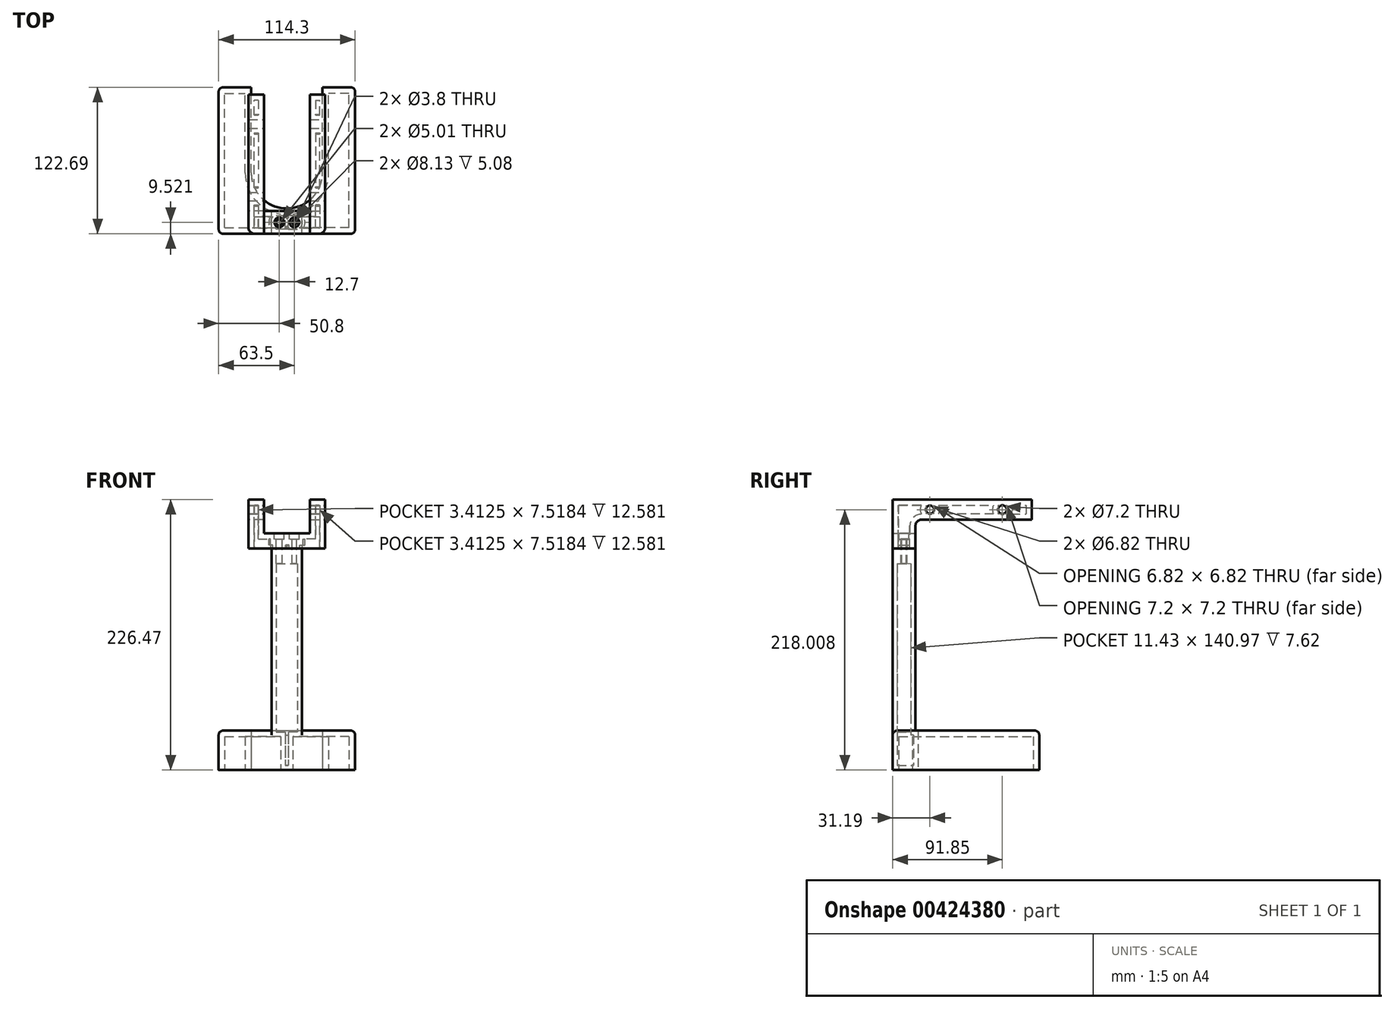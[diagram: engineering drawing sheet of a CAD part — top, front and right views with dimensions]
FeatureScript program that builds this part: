
annotation { "Feature Type Name" : "Feature", "Feature Type Description" : "" }
export const myFeature = defineFeature(function(context is Context, id is Id, definition is map)
    precondition{}
    {
        {
            var Q0;
            Q0=qCreatedBy(makeId("Top.planeOp"),FACE);
            var sketch = newSketch(context, id + "F0", { "sketchPlane" : qUnion([Q0])});
            skLineSegment(sketch, "E0", {"start": v(57.15, -21.2) * mm, "end": v(57.15, 101.5) * mm});
            skLineSegment(sketch, "E1", {"start": v(29.87, 29.87) * mm, "end": v(29.87, 101.5) * mm});
            skLineSegment(sketch, "E2", {"start": v(57.15, 101.5) * mm, "end": v(29.87, 101.5) * mm});
            skLineSegment(sketch, "E3", {"start": v(57.15, -21.2) * mm, "end": v(0, -21.2) * mm});
            skLineSegment(sketch, "E4", {"start": v(0, -21.2) * mm, "end": v(0, 0) * mm});
            skPoint(sketch, "E5.center.orphan", {"position": v(0, 29.87) * mm});
            skArc(sketch, "E6", {"start": v(0, 0) * mm, "mid": v(21.12, 8.75) * mm, "end": v(29.87, 29.87) * mm});
            skSolve(sketch);
        }
        {
            var Q0;
            Q0=makeQuery(id+"F0.imprint","IMPRINT",FACE,{"disambiguationData":[TD([[makeQuery(id+"F0.imprint","IMPRINT",EDGE,{"derivedFrom":sQuery(id+"F0.wireOp",EDGE,"E0")}),1.0]])]});
            extrude(context, id + "F1", {"entities" : qUnion([Q0]), "depth" : 33.02 * mm});
        }
        {
            var Q0;
            Q0=makeQuery(id+"F1.opExtrude","CAP_FACE",FACE,{"disambiguationData":[OSD([sQuery(id+"F0.wireOp",EDGE,"E0"),sQuery(id+"F0.wireOp",EDGE,"E1"),sQuery(id+"F0.wireOp",EDGE,"E2"),sQuery(id+"F0.wireOp",EDGE,"E3"),sQuery(id+"F0.wireOp",EDGE,"E4"),sQuery(id+"F0.wireOp",EDGE,"E6")])],"isStart":true});
            shell(context, id + "F2", {"entities" : qUnion([Q0]), "thickness" : 5.08 * mm});
        }
        {
            var Q0;
            Q0=makeQuery(id+"F1.opExtrude","CAP_FACE",FACE,{"disambiguationData":[OSD([sQuery(id+"F0.wireOp",EDGE,"E0"),sQuery(id+"F0.wireOp",EDGE,"E1"),sQuery(id+"F0.wireOp",EDGE,"E2"),sQuery(id+"F0.wireOp",EDGE,"E3"),sQuery(id+"F0.wireOp",EDGE,"E4"),sQuery(id+"F0.wireOp",EDGE,"E6")])],"isStart":false});
            var sketch = newSketch(context, id + "F3", { "sketchPlane" : qUnion([Q0])});
            skLineSegment(sketch, "E7.bottom", {"start": v(0, -21.2) * mm, "end": v(12.7, -21.2) * mm});
            skLineSegment(sketch, "E7.top", {"start": v(0, -2.14) * mm, "end": v(12.7, -2.14) * mm});
            skLineSegment(sketch, "E7.left", {"start": v(0, -21.2) * mm, "end": v(0, -2.14) * mm});
            skLineSegment(sketch, "E7.right", {"start": v(12.7, -21.2) * mm, "end": v(12.7, -2.14) * mm});
            skSolve(sketch);
        }
        {
            var Q0;
            Q0=makeQuery(id+"F3.imprint","IMPRINT",FACE,{"disambiguationData":[TD([[makeQuery(id+"F3.imprint","IMPRINT",EDGE,{"derivedFrom":sQuery(id+"F3.wireOp",EDGE,"E7.bottom")}),-1.0]])]});
            extrude(context, id + "F4", {"entities" : qUnion([Q0]), "operationType" : NewBodyOperationType.ADD, "depth" : 152.4 * mm});
        }
        {
            var Q0;
            Q0=makeQuery(id+"F4.opExtrude","CAP_EDGE",EDGE,{"disambiguationData":[OSD([sQuery(id+"F3.wireOp",EDGE,"E7.top")])],"isStart":true});
            var Q1;
            Q1=makeQuery(id+"F4.opExtrude","CAP_EDGE",EDGE,{"disambiguationData":[OSD([sQuery(id+"F3.wireOp",EDGE,"E7.right")])],"isStart":true});
            var Q2;
            Q2=makeQuery(id+"F1.opExtrude","CAP_EDGE",EDGE,{"disambiguationData":[OSD([sQuery(id+"F0.wireOp",EDGE,"E3")])],"isStart":false});
            var Q3;
            Q3=makeQuery(id+"F1.opExtrude","CAP_EDGE",EDGE,{"disambiguationData":[OSD([sQuery(id+"F0.wireOp",EDGE,"E0")])],"isStart":false});
            var Q4;
            Q4=makeQuery(id+"F1.opExtrude","CAP_EDGE",EDGE,{"disambiguationData":[OSD([sQuery(id+"F0.wireOp",EDGE,"E2")])],"isStart":false});
            var Q5;
            Q5=makeQuery(id+"F1.opExtrude","SWEPT_EDGE",EDGE,{"disambiguationData":[OSD([sQuery(id+"F0.wireOp",EDGE,"E0"),sQuery(id+"F0.wireOp",EDGE,"E3")])]});
            var Q6;
            Q6=makeQuery(id+"F1.opExtrude","SWEPT_EDGE",EDGE,{"disambiguationData":[OSD([sQuery(id+"F0.wireOp",EDGE,"E0"),sQuery(id+"F0.wireOp",EDGE,"E2")])]});
            fillet(context, id + "F5", {"entities" : qUnion([Q0, Q1, Q2, Q3, Q4, Q5, Q6]), "radius" : 3.8 * mm, "tangentPropagation" : true, "allowEdgeOverflow" : false});
        }
        {
            var Q0;
            Q0=makeQuery(id+"F1.opExtrude","SWEPT_BODY",BODY,{"disambiguationData":[OSD([sQuery(id+"F0.wireOp",EDGE,"E0"),sQuery(id+"F0.wireOp",EDGE,"E1"),sQuery(id+"F0.wireOp",EDGE,"E2"),sQuery(id+"F0.wireOp",EDGE,"E3"),sQuery(id+"F0.wireOp",EDGE,"E4"),sQuery(id+"F0.wireOp",EDGE,"E6")])]});
            var Q1;
            Q1=makeQuery(id+"F4.boolean.opBoolean","MERGE",FACE,{"derivedFrom":[makeQuery(id+"F1.opExtrude","SWEPT_FACE",FACE,{"disambiguationData":[OSD([sQuery(id+"F0.wireOp",EDGE,"E4")])]}),makeQuery(id+"F4.opExtrude","SWEPT_FACE",FACE,{"disambiguationData":[OSD([sQuery(id+"F3.wireOp",EDGE,"E7.left")])]})]});
            mirror(context, id + "F6", {"operationType" : NewBodyOperationType.ADD, "entities" : qUnion([Q0]), "mirrorPlane" : qUnion([Q1])});
        }
        {
            var Q0;
            {var subQ0=makeQuery(id+"F4.opExtrude","CAP_FACE",FACE,{"disambiguationData":[OSD([sQuery(id+"F3.wireOp",EDGE,"E7.bottom"),sQuery(id+"F3.wireOp",EDGE,"E7.top"),sQuery(id+"F3.wireOp",EDGE,"E7.left"),sQuery(id+"F3.wireOp",EDGE,"E7.right")])],"isStart":false});Q0=makeQuery(id+"F6.boolean.opBoolean","MERGE",FACE,{"derivedFrom":[subQ0,makeQuery(id+"F6.opPattern","COPY",FACE,{"derivedFrom":subQ0,"instanceName":"1"})]});}
            shell(context, id + "F7", {"entities" : qUnion([Q0]), "thickness" : 3.8 * mm});
        }
        {
            var Q0;
            {var subQ0=makeQuery(id+"F4.opExtrude","CAP_FACE",FACE,{"disambiguationData":[OSD([sQuery(id+"F3.wireOp",EDGE,"E7.bottom"),sQuery(id+"F3.wireOp",EDGE,"E7.top"),sQuery(id+"F3.wireOp",EDGE,"E7.left"),sQuery(id+"F3.wireOp",EDGE,"E7.right")])],"isStart":false});Q0=makeQuery(id+"F6.boolean.opBoolean","MERGE",FACE,{"derivedFrom":[subQ0,makeQuery(id+"F6.opPattern","COPY",FACE,{"derivedFrom":subQ0,"instanceName":"1"})]});}
            var sketch = newSketch(context, id + "F8", { "sketchPlane" : qUnion([Q0])});
            skLineSegment(sketch, "E8.0", {"start": v(-8.9, -17.38) * mm, "end": v(-8.9, -5.95) * mm});
            skLineSegment(sketch, "E9.0", {"start": v(-8.89, -5.95) * mm, "end": v(8.89, -5.95) * mm});
            skLineSegment(sketch, "E10.0", {"start": v(8.89, -17.38) * mm, "end": v(-8.89, -17.38) * mm});
            skLineSegment(sketch, "E11.0", {"start": v(8.9, -17.38) * mm, "end": v(8.89, -5.95) * mm});
            skSolve(sketch);
        }
        {
            var Q0;
            Q0=makeQuery(id+"F8.imprint","IMPRINT",FACE,{"disambiguationData":[TD([[makeQuery(id+"F8.imprint","IMPRINT",EDGE,{"derivedFrom":sQuery(id+"F8.wireOp",EDGE,"E8.0")}),-1.0]])]});
            extrude(context, id + "F9", {"entities" : qUnion([Q0]), "operationType" : NewBodyOperationType.ADD, "oppositeDirection" : true, "depth" : 12.7 * mm});
        }
        {
            var Q0;
            {var subQ0=makeQuery(id+"F4.opExtrude","CAP_FACE",FACE,{"disambiguationData":[OSD([sQuery(id+"F3.wireOp",EDGE,"E7.bottom"),sQuery(id+"F3.wireOp",EDGE,"E7.top"),sQuery(id+"F3.wireOp",EDGE,"E7.left"),sQuery(id+"F3.wireOp",EDGE,"E7.right")])],"isStart":false});Q0=makeQuery(id+"F9.boolean.opBoolean","MERGE",FACE,{"derivedFrom":[makeQuery(id+"F6.boolean.opBoolean","MERGE",FACE,{"derivedFrom":[subQ0,makeQuery(id+"F6.opPattern","COPY",FACE,{"derivedFrom":subQ0,"instanceName":"1"})]}),makeQuery(id+"F9.opExtrude","CAP_FACE",FACE,{"disambiguationData":[OSD([sQuery(id+"F8.wireOp",EDGE,"E8.0"),sQuery(id+"F8.wireOp",EDGE,"E9.0"),sQuery(id+"F8.wireOp",EDGE,"E10.0"),sQuery(id+"F8.wireOp",EDGE,"E11.0")])],"isStart":true})]});}
            var sketch = newSketch(context, id + "F10", { "sketchPlane" : qUnion([Q0])});
            skLineSegment(sketch, "E12", {"start": v(0, -2.14) * mm, "end": v(19.28, -2.14) * mm});
            skLineSegment(sketch, "E13", {"start": v(19.28, -2.14) * mm, "end": v(19.28, 95.34) * mm});
            skLineSegment(sketch, "E14", {"start": v(19.28, 95.34) * mm, "end": v(32.1, 95.34) * mm});
            skLineSegment(sketch, "E15", {"start": v(32.1, 95.34) * mm, "end": v(32.1, -21.2) * mm});
            skLineSegment(sketch, "E16", {"start": v(32.1, -21.2) * mm, "end": v(0, -21.2) * mm});
            skLineSegment(sketch, "E17", {"start": v(0, -21.2) * mm, "end": v(0, -2.14) * mm});
            skSolve(sketch);
        }
        {
            var Q0;
            {var subQ1=sQuery(id+"F10.wireOp",EDGE,"E13");Q0=makeQuery(id+"F10.imprint","IMPRINT",FACE,{"disambiguationData":[TD([[makeQuery(id+"F10.imprint","IMPRINT",EDGE,{"derivedFrom":subQ1}),-1.0]])]});}
            var Q1;
            {var subQ4=sQuery(id+"F10.wireOp",EDGE,"E17");Q1=makeQuery(id+"F10.imprint","IMPRINT",FACE,{"disambiguationData":[TD([[makeQuery(id+"F10.imprint","IMPRINT",EDGE,{"derivedFrom":subQ4}),-1.0]])]});}
            extrude(context, id + "F11", {"entities" : qUnion([Q0, Q1]), "depth" : 43.18 * mm});
        }
        {
            var Q0;
            Q0=makeQuery(id+"F11.opExtrude","SWEPT_FACE",FACE,{"disambiguationData":[OSD([sQuery(id+"F10.wireOp",EDGE,"E15")])]});
            var sketch = newSketch(context, id + "F12", { "sketchPlane" : qUnion([Q0])});
            skPoint(sketch, "E18.0", {"position": v(-2.14, 185.42) * mm});
            skLineSegment(sketch, "E19.bottom", {"start": v(-2.14, 185.42) * mm, "end": v(95.34, 185.42) * mm});
            skLineSegment(sketch, "E19.top", {"start": v(-2.14, 209.55) * mm, "end": v(95.34, 209.55) * mm});
            skLineSegment(sketch, "E19.left", {"start": v(-2.14, 185.42) * mm, "end": v(-2.14, 209.55) * mm});
            skLineSegment(sketch, "E19.right", {"start": v(95.34, 185.42) * mm, "end": v(95.34, 209.55) * mm});
            skSolve(sketch);
        }
        {
            var Q0;
            Q0=makeQuery(id+"F12.imprint","IMPRINT",FACE,{"disambiguationData":[TD([[makeQuery(id+"F12.imprint","IMPRINT",EDGE,{"derivedFrom":sQuery(id+"F12.wireOp",EDGE,"E19.bottom")}),-1.0]])]});
            extrude(context, id + "F13", {"entities" : qUnion([Q0]), "operationType" : NewBodyOperationType.REMOVE, "endBound" : BoundingType.THROUGH_ALL, "oppositeDirection" : true, "depth" : 25.4 * mm});
        }
        {
            var Q0;
            Q0=makeQuery(id+"F13.boolean.opBoolean","MERGE",FACE,{"derivedFrom":[makeQuery(id+"F11.opExtrude","SWEPT_FACE",FACE,{"disambiguationData":[OSD([sQuery(id+"F10.wireOp",EDGE,"E12")])]}),makeQuery(id+"F13.opExtrude","SWEPT_FACE",FACE,{"disambiguationData":[OSD([sQuery(id+"F12.wireOp",EDGE,"E19.left")])]})]});
            var sketch = newSketch(context, id + "F14", { "sketchPlane" : qUnion([Q0])});
            skLineSegment(sketch, "E20.bottom", {"start": v(-19.28, 228.6) * mm, "end": v(0, 228.6) * mm});
            skLineSegment(sketch, "E20.top", {"start": v(-19.28, 198.12) * mm, "end": v(0, 198.12) * mm});
            skLineSegment(sketch, "E20.left", {"start": v(-19.28, 228.6) * mm, "end": v(-19.28, 198.12) * mm});
            skLineSegment(sketch, "E20.right", {"start": v(0, 228.6) * mm, "end": v(0, 198.12) * mm});
            skSolve(sketch);
        }
        {
            var Q0;
            {var subQ1=sQuery(id+"F14.wireOp",EDGE,"E20.bottom");Q0=makeQuery(id+"F14.imprint","IMPRINT",FACE,{"disambiguationData":[TD([[makeQuery(id+"F14.imprint","IMPRINT",EDGE,{"derivedFrom":subQ1}),1.0]])]});}
            extrude(context, id + "F15", {"entities" : qUnion([Q0]), "operationType" : NewBodyOperationType.REMOVE, "oppositeDirection" : true, "depth" : 25.4 * mm});
        }
        {
            var Q0;
            Q0=makeQuery(id+"F11.opExtrude","SWEPT_EDGE",EDGE,{"disambiguationData":[OSD([sQuery(id+"F10.wireOp",EDGE,"E15"),sQuery(id+"F10.wireOp",EDGE,"E16")])]});
            var Q1;
            Q1=makeQuery(id+"F13.boolean.opBoolean","COPY",EDGE,{"derivedFrom":makeQuery(id+"F13.opExtrude","CAP_EDGE",EDGE,{"disambiguationData":[OSD([sQuery(id+"F12.wireOp",EDGE,"E19.left")])],"isStart":true})});
            fillet(context, id + "F16", {"entities" : qUnion([Q0, Q1]), "radius" : 5.08 * mm, "tangentPropagation" : true, "allowEdgeOverflow" : false});
        }
        {
            var Q0;
            Q0=makeQuery(id+"F15.boolean.opBoolean","COPY",FACE,{"derivedFrom":makeQuery(id+"F15.opExtrude","SWEPT_FACE",FACE,{"disambiguationData":[OSD([sQuery(id+"F14.wireOp",EDGE,"E20.top")])]})});
            var sketch = newSketch(context, id + "F17", { "sketchPlane" : qUnion([Q0])});
            skCircle(sketch, "E21", {"center": v(6.35, -11.67) * mm, "radius": 1.9 * mm});
            skSolve(sketch);
        }
        {
            var Q0;
            Q0=makeQuery(id+"F17.imprint","IMPRINT",FACE,{"disambiguationData":[TD([[makeQuery(id+"F17.imprint","IMPRINT",EDGE,{"derivedFrom":sQuery(id+"F17.wireOp",EDGE,"E21")}),1.0]])]});
            var Q1;
            Q1=sQuery(id+"F17.wireOp",EDGE,"E21");
            extrude(context, id + "F18", {"entities" : qUnion([Q0]), "operationType" : NewBodyOperationType.REMOVE, "surfaceEntities" : qUnion([Q1]), "oppositeDirection" : true, "depth" : 79 * mm});
        }
        {
            var Q0;
            Q0=qCreatedBy(makeId("Front.planeOp"),FACE);
            var sketch = newSketch(context, id + "F19", { "sketchPlane" : qUnion([Q0])});
            skLineSegment(sketch, "E22.bottom", {"start": v(0, 210.43) * mm, "end": v(-135.66, 210.43) * mm});
            skLineSegment(sketch, "E22.top", {"start": v(0, -60.9) * mm, "end": v(-135.66, -60.9) * mm});
            skLineSegment(sketch, "E22.left", {"start": v(0, 210.43) * mm, "end": v(0, -60.9) * mm});
            skLineSegment(sketch, "E22.right", {"start": v(-135.66, 210.43) * mm, "end": v(-135.66, -60.9) * mm});
            skSolve(sketch);
        }
        {
            var Q0;
            Q0=makeQuery(id+"F19.imprint","IMPRINT",FACE,{"disambiguationData":[TD([[makeQuery(id+"F19.imprint","IMPRINT",EDGE,{"derivedFrom":sQuery(id+"F19.wireOp",EDGE,"E22.bottom")}),1.0]])]});
            extrude(context, id + "F20", {"entities" : qUnion([Q0]), "operationType" : NewBodyOperationType.REMOVE, "depth" : 127 * mm, "hasSecondDirection" : true, "secondDirectionOppositeDirection" : true, "secondDirectionDepth" : 127 * mm});
        }
        {
            var Q0;
            Q0=makeQuery(id+"F11.opExtrude","SWEPT_BODY",BODY,{"disambiguationData":[OSD([sQuery(id+"F10.wireOp",EDGE,"E12"),sQuery(id+"F10.wireOp",EDGE,"E13"),sQuery(id+"F10.wireOp",EDGE,"E14"),sQuery(id+"F10.wireOp",EDGE,"E15"),sQuery(id+"F10.wireOp",EDGE,"E16"),sQuery(id+"F10.wireOp",EDGE,"E17")])]});
            var Q1;
            Q1=makeQuery(id+"F1.opExtrude","SWEPT_BODY",BODY,{"disambiguationData":[OSD([sQuery(id+"F0.wireOp",EDGE,"E0"),sQuery(id+"F0.wireOp",EDGE,"E1"),sQuery(id+"F0.wireOp",EDGE,"E2"),sQuery(id+"F0.wireOp",EDGE,"E3"),sQuery(id+"F0.wireOp",EDGE,"E4"),sQuery(id+"F0.wireOp",EDGE,"E6")])]});
            var Q2;
            Q2=makeQuery(id+"F11.opExtrude","SWEPT_FACE",FACE,{"disambiguationData":[OSD([sQuery(id+"F10.wireOp",EDGE,"E17")])]});
            mirror(context, id + "F21", {"entities" : qUnion([Q0, Q1]), "mirrorPlane" : qUnion([Q2])});
        }
        {
            var Q0;
            Q0=makeQuery(id+"F1.opExtrude","SWEPT_BODY",BODY,{"disambiguationData":[OSD([sQuery(id+"F0.wireOp",EDGE,"E0"),sQuery(id+"F0.wireOp",EDGE,"E1"),sQuery(id+"F0.wireOp",EDGE,"E2"),sQuery(id+"F0.wireOp",EDGE,"E3"),sQuery(id+"F0.wireOp",EDGE,"E4"),sQuery(id+"F0.wireOp",EDGE,"E6")])]});
            var Q1;
            Q1=makeQuery(id+"F21.opPattern","COPY",BODY,{"derivedFrom":makeQuery(id+"F1.opExtrude","SWEPT_BODY",BODY,{"disambiguationData":[OSD([sQuery(id+"F0.wireOp",EDGE,"E0"),sQuery(id+"F0.wireOp",EDGE,"E1"),sQuery(id+"F0.wireOp",EDGE,"E2"),sQuery(id+"F0.wireOp",EDGE,"E3"),sQuery(id+"F0.wireOp",EDGE,"E4"),sQuery(id+"F0.wireOp",EDGE,"E6")])]}),"instanceName":"1"});
            booleanBodies(context, id + "F22", {"operationType" : BooleanOperationType.UNION, "tools" : qUnion([Q0, Q1])});
        }
        {
            var Q0;
            Q0=makeQuery(id+"F11.opExtrude","SWEPT_BODY",BODY,{"disambiguationData":[OSD([sQuery(id+"F10.wireOp",EDGE,"E12"),sQuery(id+"F10.wireOp",EDGE,"E13"),sQuery(id+"F10.wireOp",EDGE,"E14"),sQuery(id+"F10.wireOp",EDGE,"E15"),sQuery(id+"F10.wireOp",EDGE,"E16"),sQuery(id+"F10.wireOp",EDGE,"E17")])]});
            var Q1;
            Q1=makeQuery(id+"F21.opPattern","COPY",BODY,{"derivedFrom":makeQuery(id+"F11.opExtrude","SWEPT_BODY",BODY,{"disambiguationData":[OSD([sQuery(id+"F10.wireOp",EDGE,"E12"),sQuery(id+"F10.wireOp",EDGE,"E13"),sQuery(id+"F10.wireOp",EDGE,"E14"),sQuery(id+"F10.wireOp",EDGE,"E15"),sQuery(id+"F10.wireOp",EDGE,"E16"),sQuery(id+"F10.wireOp",EDGE,"E17")])]}),"instanceName":"1"});
            booleanBodies(context, id + "F23", {"operationType" : BooleanOperationType.UNION, "tools" : qUnion([Q0, Q1])});
        }
        {
            var Q0;
            Q0=makeQuery(id+"F11.opExtrude","SWEPT_FACE",FACE,{"disambiguationData":[OSD([sQuery(id+"F10.wireOp",EDGE,"E15")])]});
            var sketch = newSketch(context, id + "F24", { "sketchPlane" : qUnion([Q0])});
            skLineSegment(sketch, "E23", {"start": v(0, 0) * mm, "end": v(0, 33.4) * mm, "construction": true});
            skCircle(sketch, "E24", {"center": v(10, 218) * mm, "radius": 3.4 * mm});
            skCircle(sketch, "E25", {"center": v(70.66, 218) * mm, "radius": 3.6 * mm});
            skPoint(sketch, "E25.centerSnap0", {"position": v(95.34, 218) * mm});
            skSolve(sketch);
        }
        {
            var Q0;
            Q0=makeQuery(id+"F24.imprint","IMPRINT",FACE,{"disambiguationData":[TD([[makeQuery(id+"F24.imprint","IMPRINT",EDGE,{"derivedFrom":sQuery(id+"F24.wireOp",EDGE,"E24")}),1.0]])]});
            var Q1;
            Q1=makeQuery(id+"F24.imprint","IMPRINT",FACE,{"disambiguationData":[TD([[makeQuery(id+"F24.imprint","IMPRINT",EDGE,{"derivedFrom":sQuery(id+"F24.wireOp",EDGE,"E25")}),1.0]])]});
            extrude(context, id + "F25", {"entities" : qUnion([Q0, Q1]), "operationType" : NewBodyOperationType.REMOVE, "endBound" : BoundingType.THROUGH_ALL, "oppositeDirection" : true, "depth" : 25.4 * mm});
        }
        {
            var Q0;
            Q0=makeQuery(id+"F13.boolean.opBoolean","COPY",EDGE,{"derivedFrom":makeQuery(id+"F13.opExtrude","SWEPT_EDGE",EDGE,{"disambiguationData":[OSD([sQuery(id+"F12.wireOp",EDGE,"E19.top"),sQuery(id+"F12.wireOp",EDGE,"E19.left")])]})});
            var Q1;
            Q1=makeQuery(id+"F21.opPattern","COPY",EDGE,{"derivedFrom":makeQuery(id+"F13.boolean.opBoolean","COPY",EDGE,{"derivedFrom":makeQuery(id+"F13.opExtrude","SWEPT_EDGE",EDGE,{"disambiguationData":[OSD([sQuery(id+"F12.wireOp",EDGE,"E19.top"),sQuery(id+"F12.wireOp",EDGE,"E19.left")])]})}),"instanceName":"1"});
            fillet(context, id + "F26", {"entities" : qUnion([Q0, Q1]), "radius" : 5.08 * mm, "tangentPropagation" : true, "allowEdgeOverflow" : false});
        }
        {
            var Q0;
            Q0=makeQuery(id+"F11.opExtrude","SWEPT_FACE",FACE,{"disambiguationData":[OSD([sQuery(id+"F10.wireOp",EDGE,"E15")])]});
            var sketch = newSketch(context, id + "F27", { "sketchPlane" : qUnion([Q0])});
            skLineSegment(sketch, "E26.bottom", {"start": v(95.34, 228.6) * mm, "end": v(-21.62, 228.6) * mm});
            skLineSegment(sketch, "E26.top", {"start": v(95.34, 226.47) * mm, "end": v(-21.62, 226.47) * mm});
            skLineSegment(sketch, "E26.left", {"start": v(95.34, 228.6) * mm, "end": v(95.34, 226.47) * mm});
            skLineSegment(sketch, "E26.right", {"start": v(-21.62, 228.6) * mm, "end": v(-21.62, 226.47) * mm});
            skSolve(sketch);
        }
        {
            var Q0;
            {var subQ0=sQuery(id+"F27.wireOp",EDGE,"E26.left");Q0=makeQuery(id+"F27.imprint","IMPRINT",FACE,{"disambiguationData":[TD([[makeQuery(id+"F27.imprint","IMPRINT",EDGE,{"derivedFrom":subQ0}),-1.0]])]});}
            var Q1;
            {var subQ4=sQuery(id+"F27.wireOp",EDGE,"E26.right");Q1=makeQuery(id+"F27.imprint","IMPRINT",FACE,{"disambiguationData":[TD([[makeQuery(id+"F27.imprint","IMPRINT",EDGE,{"derivedFrom":subQ4}),1.0]])]});}
            extrude(context, id + "F28", {"entities" : qUnion([Q0, Q1]), "operationType" : NewBodyOperationType.REMOVE, "endBound" : BoundingType.THROUGH_ALL, "oppositeDirection" : true, "depth" : 25.4 * mm});
        }
        {
            var Q0;
            {var subQ0=makeQuery(id+"F15.boolean.opBoolean","COPY",FACE,{"derivedFrom":makeQuery(id+"F15.opExtrude","SWEPT_FACE",FACE,{"disambiguationData":[OSD([sQuery(id+"F14.wireOp",EDGE,"E20.top")])]})});Q0=makeQuery(id+"F23.opBoolean","MERGE",FACE,{"derivedFrom":[subQ0,makeQuery(id+"F21.opPattern","COPY",FACE,{"derivedFrom":subQ0,"instanceName":"1"})]});}
            var sketch = newSketch(context, id + "F29", { "sketchPlane" : qUnion([Q0])});
            skCircle(sketch, "E27", {"center": v(-6.35, -11.67) * mm, "radius": 4.06 * mm});
            skCircle(sketch, "E28", {"center": v(6.35, -11.67) * mm, "radius": 4.06 * mm});
            skSolve(sketch);
        }
        {
            var Q0;
            Q0=makeQuery(id+"F29.imprint","IMPRINT",FACE,{"disambiguationData":[TD([[makeQuery(id+"F29.imprint","IMPRINT",EDGE,{"derivedFrom":sQuery(id+"F29.wireOp",EDGE,"E27")}),1.0]])]});
            var Q1;
            Q1=makeQuery(id+"F29.imprint","IMPRINT",FACE,{"disambiguationData":[TD([[makeQuery(id+"F29.imprint","IMPRINT",EDGE,{"derivedFrom":sQuery(id+"F29.wireOp",EDGE,"E28")}),1.0]])]});
            extrude(context, id + "F30", {"entities" : qUnion([Q0, Q1]), "operationType" : NewBodyOperationType.REMOVE, "oppositeDirection" : true, "depth" : 5.08 * mm});
        }
        {
            var Q0;
            Q0=makeQuery(id+"F30.boolean.opBoolean","COPY",FACE,{"derivedFrom":makeQuery(id+"F30.opExtrude","CAP_FACE",FACE,{"disambiguationData":[OSD([sQuery(id+"F17.wireOp",EDGE,"E21"),sQuery(id+"F29.wireOp",EDGE,"E27")])],"isStart":false})});
            var sketch = newSketch(context, id + "F31", { "sketchPlane" : qUnion([Q0])});
            skCircle(sketch, "E29", {"center": v(-6.35, -11.67) * mm, "radius": 2.5 * mm});
            skCircle(sketch, "E30.MirrorC", {"center": v(6.35, -11.67) * mm, "radius": 2.5 * mm});
            skSolve(sketch);
        }
        {
            var Q0;
            Q0=makeQuery(id+"F31.imprint","IMPRINT",FACE,{"disambiguationData":[TD([[makeQuery(id+"F31.imprint","IMPRINT",EDGE,{"derivedFrom":sQuery(id+"F31.wireOp",EDGE,"E29")}),1.0]])]});
            var Q1;
            Q1=makeQuery(id+"F31.imprint","IMPRINT",FACE,{"disambiguationData":[TD([[makeQuery(id+"F31.imprint","IMPRINT",EDGE,{"derivedFrom":sQuery(id+"F31.wireOp",EDGE,"E30.MirrorC")}),-1.0]])]});
            extrude(context, id + "F32", {"entities" : qUnion([Q0, Q1]), "operationType" : NewBodyOperationType.REMOVE, "oppositeDirection" : true, "depth" : 25.4 * mm});
        }
        {
            var Q0;
            {var subQ0=makeQuery(id+"F11.opExtrude","CAP_FACE",FACE,{"disambiguationData":[OSD([sQuery(id+"F10.wireOp",EDGE,"E12"),sQuery(id+"F10.wireOp",EDGE,"E13"),sQuery(id+"F10.wireOp",EDGE,"E14"),sQuery(id+"F10.wireOp",EDGE,"E15"),sQuery(id+"F10.wireOp",EDGE,"E16"),sQuery(id+"F10.wireOp",EDGE,"E17")])],"isStart":true});Q0=makeQuery(id+"F23.opBoolean","MERGE",FACE,{"derivedFrom":[subQ0,makeQuery(id+"F21.opPattern","COPY",FACE,{"derivedFrom":subQ0,"instanceName":"1"})]});}
            shell(context, id + "F33", {"entities" : qUnion([Q0]), "thickness" : 4.7 * mm});
        }
    });
